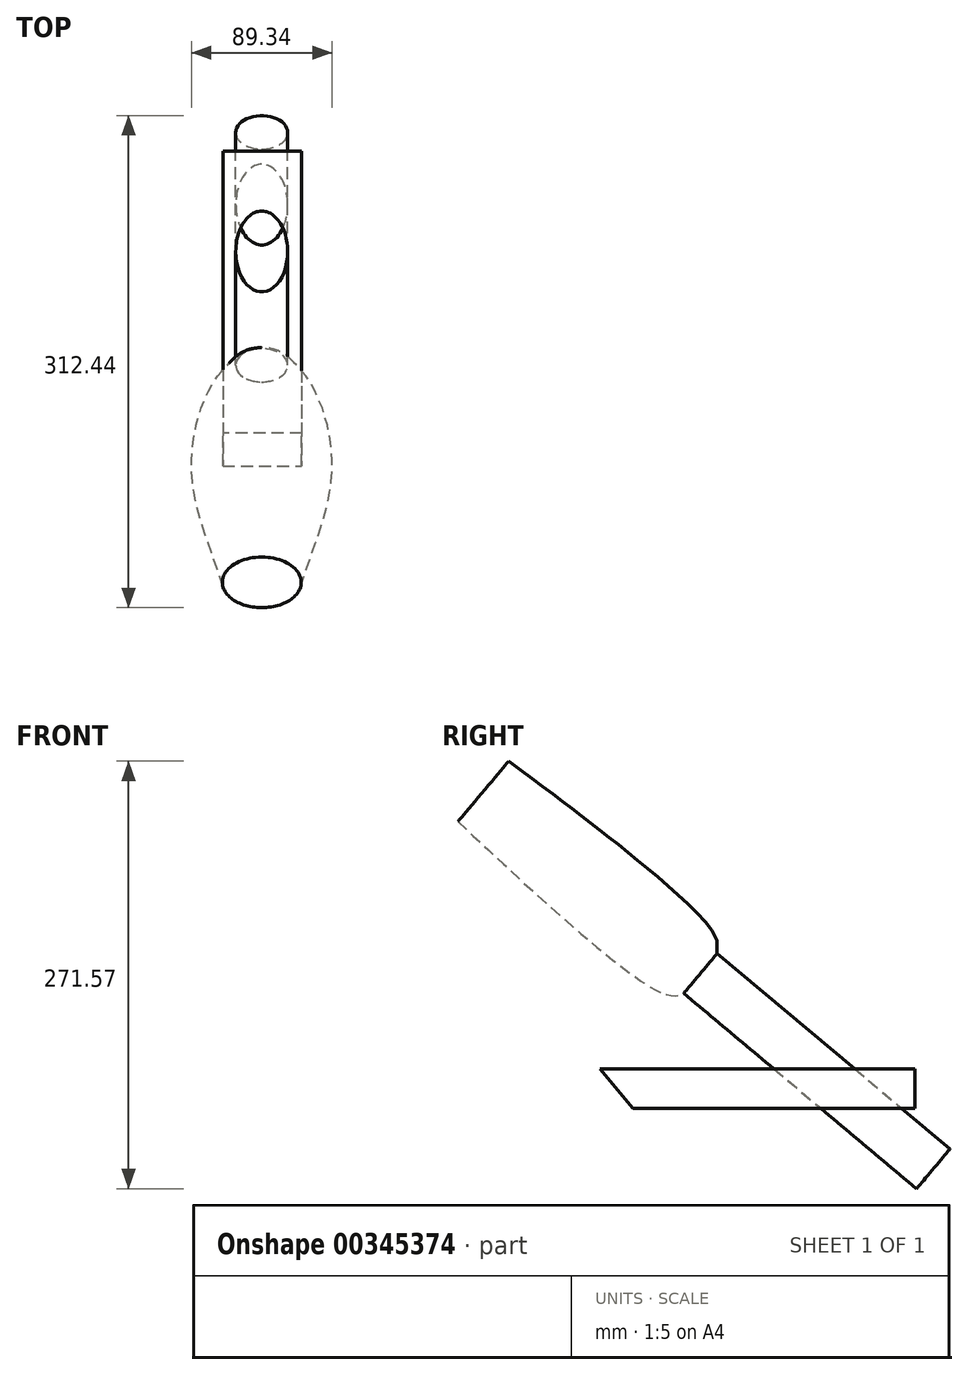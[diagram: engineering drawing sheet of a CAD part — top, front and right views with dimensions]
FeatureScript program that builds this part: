
annotation { "Feature Type Name" : "Feature", "Feature Type Description" : "" }
export const myFeature = defineFeature(function(context is Context, id is Id, definition is map)
    precondition{}
    {
        {
            var Q0;
            Q0=qCreatedBy(makeId("Top.planeOp"),FACE);
            var sketch = newSketch(context, id + "F0", { "sketchPlane" : qUnion([Q0])});
            skLineSegment(sketch, "E0.bottom", {"start": v(-24.67, 141.07) * mm, "end": v(25.33, 141.07) * mm});
            skLineSegment(sketch, "E0.top", {"start": v(-24.67, -58.93) * mm, "end": v(25.33, -58.93) * mm});
            skLineSegment(sketch, "E0.left", {"start": v(-24.67, 141.07) * mm, "end": v(-24.67, -58.93) * mm});
            skLineSegment(sketch, "E0.right", {"start": v(25.33, 141.07) * mm, "end": v(25.33, -58.93) * mm});
            skSolve(sketch);
        }
        {
            var Q0;
            Q0 = qSketchRegion(id + "F0", true);
            extrude(context, id + "F1", {"entities" : qUnion([Q0]), "depth" : 25 * mm});
        }
        {
            var Q0;
            Q0=makeQuery(id+"F1.opExtrude","SWEPT_FACE",FACE,{"disambiguationData":[OSD([sQuery(id+"F0.wireOp",EDGE,"E0.left")])]});
            var sketch = newSketch(context, id + "F2", { "sketchPlane" : qUnion([Q0])});
            skLineSegment(sketch, "E1", {"start": v(58.93, 25) * mm, "end": v(37.96, 0) * mm});
            skLineSegment(sketch, "E2", {"start": v(37.96, 0) * mm, "end": v(58.93, 0) * mm});
            skLineSegment(sketch, "E3", {"start": v(58.93, 0) * mm, "end": v(58.93, 25) * mm});
            skSolve(sketch);
        }
        {
            var Q0;
            Q0=makeQuery(id+"F2.imprint","IMPRINT",FACE,{"disambiguationData":[TD([[makeQuery(id+"F2.imprint","IMPRINT",EDGE,{"derivedFrom":sQuery(id+"F2.wireOp",EDGE,"E1")}),1.0]])]});
            extrude(context, id + "F3", {"entities" : qUnion([Q0]), "operationType" : NewBodyOperationType.REMOVE, "endBound" : BoundingType.UP_TO_NEXT, "oppositeDirection" : true, "depth" : 25 * mm});
        }
        {
            var Q0;
            Q0=qCreatedBy(makeId("Right.planeOp"),FACE);
            var sketch = newSketch(context, id + "F4", { "sketchPlane" : qUnion([Q0])});
            skLineSegment(sketch, "E4", {"start": v(152.85, -38.43) * mm, "end": v(4.97, 85.66) * mm});
            skSolve(sketch);
        }
        {
            var Q0;
            Q0=sQuery(id+"F4.wireOp",EDGE,"E4");
            var Q1;
            Q1=sQuery(id+"F4.wireOp",VERTEX,"E4.end");
            cPlane(context, id + "F5", {"entities" : qUnion([Q0, Q1]), "cplaneType" : CPlaneType.LINE_POINT, "offset" : 25 * mm, "width" : 150 * mm, "height" : 150 * mm});
        }
        {
            var Q0;
            Q0=qCreatedBy(id+"F5.planeOp",FACE);
            var sketch = newSketch(context, id + "F6", { "sketchPlane" : qUnion([Q0])});
            skPoint(sketch, "E5.0", {"position": v(0, 68.81) * mm});
            skCircle(sketch, "E6", {"center": v(0, 68.81) * mm, "radius": 16.5 * mm});
            skSolve(sketch);
        }
        {
            var Q0;
            Q0=makeQuery(id+"F6.imprint","IMPRINT",FACE,{"disambiguationData":[TD([[makeQuery(id+"F6.imprint","IMPRINT",EDGE,{"derivedFrom":sQuery(id+"F6.wireOp",EDGE,"E6")}),1.0]])]});
            var Q1;
            Q1=sQuery(id+"F4.wireOp",EDGE,"E4");
            sweep(context, id + "F7", {"profiles" : qUnion([Q0]), "path" : qUnion([Q1])});
        }
        {
            var Q0;
            Q0=makeQuery(id+"F7.opSweep","CAP_FACE",FACE,{"disambiguationData":[OSD([sQuery(id+"F4.wireOp",VERTEX,"E4.end"),sQuery(id+"F6.wireOp",EDGE,"E6")])],"isStart":true});
            cPlane(context, id + "F8", {"entities" : qUnion([Q0]), "cplaneType" : CPlaneType.OFFSET, "offset" : 10 * mm, "width" : 150 * mm, "height" : 150 * mm});
        }
        {
            var Q0;
            Q0=qCreatedBy(id+"F8.planeOp",FACE);
            var sketch = newSketch(context, id + "F9", { "sketchPlane" : qUnion([Q0])});
            skCircle(sketch, "E7.0.0", {"center": v(0, 68.81) * mm, "radius": 16.5 * mm, "construction": true});
            skCircle(sketch, "E8", {"center": v(0, 68.81) * mm, "radius": 25 * mm});
            skSolve(sketch);
        }
        {
            var Q0;
            Q0=qCreatedBy(id+"F8.planeOp",FACE);
            cPlane(context, id + "F10", {"entities" : qUnion([Q0]), "cplaneType" : CPlaneType.OFFSET, "offset" : 170 * mm, "width" : 150 * mm, "height" : 150 * mm});
        }
        {
            var Q0;
            Q0=qCreatedBy(id+"F10.planeOp",FACE);
            var sketch = newSketch(context, id + "F11", { "sketchPlane" : qUnion([Q0])});
            skPoint(sketch, "E9.0", {"position": v(0, 68.81) * mm});
            skCircle(sketch, "E10", {"center": v(0, 68.81) * mm, "radius": 25 * mm});
            skSolve(sketch);
        }
        {
            var Q0;
            Q0=qCreatedBy(makeId("Right.planeOp"),FACE);
            var sketch = newSketch(context, id + "F12", { "sketchPlane" : qUnion([Q0])});
            skLineSegment(sketch, "E11.0", {"start": v(15.58, 98.3) * mm, "end": v(-5.63, 73.02) * mm});
            skLineSegment(sketch, "E12.0.0", {"start": v(-18.76, 72.93) * mm, "end": v(13.38, 111.24) * mm});
            skLineSegment(sketch, "E13.0", {"start": v(-148.98, 182.2) * mm, "end": v(-116.84, 220.5) * mm});
            skFitSpline(sketch, "E14", {"points": [v(15.58, 98.3) * mm, v(13.38, 111.24) * mm, v(-116.84, 220.5) * mm], "startDerivative": vector(12.66, 54.22) * mm, "endDerivative": vector(-230.77, 171) * mm});
            skFitSpline(sketch, "E15", {"points": [v(-5.63, 73.02) * mm, v(-18.76, 72.93) * mm, v(-148.98, 182.2) * mm], "startDerivative": vector(-51.2, -21.88) * mm, "endDerivative": vector(-208.48, 197.56) * mm});
            skSolve(sketch);
        }
        {
            var Q0;
            Q0=makeQuery(id+"F7.opSweep","CAP_FACE",FACE,{"disambiguationData":[OSD([sQuery(id+"F4.wireOp",VERTEX,"E4.end"),sQuery(id+"F6.wireOp",EDGE,"E6")])],"isStart":true});
            var Q1;
            Q1=makeQuery(id+"F9.imprint","IMPRINT",FACE,{"disambiguationData":[TD([[makeQuery(id+"F9.imprint","IMPRINT",EDGE,{"derivedFrom":sQuery(id+"F9.wireOp",EDGE,"E8")}),1.0]])]});
            var Q2;
            Q2=makeQuery(id+"F11.imprint","IMPRINT",FACE,{"disambiguationData":[TD([[makeQuery(id+"F11.imprint","IMPRINT",EDGE,{"derivedFrom":sQuery(id+"F11.wireOp",EDGE,"E10")}),1.0]])]});
            var Q3;
            Q3=sQuery(id+"F12.wireOp",EDGE,"E14");
            var Q4;
            Q4=sQuery(id+"F12.wireOp",EDGE,"E15");
            loft(context, id + "F13", {"addGuides" : true, "sheetProfilesArray" : [{ "sheetProfileEntities" : qUnion([Q0]) }, { "sheetProfileEntities" : qUnion([Q1]) }, { "sheetProfileEntities" : qUnion([Q2]) }], "guidesArray" : [{ "guideEntities" : qUnion([Q3]), "guideDerivativeType" : LoftGuideDerivativeType.DEFAULT, "guideDerivativeMagnitude" : 1 }, { "guideEntities" : qUnion([Q4]), "guideDerivativeType" : LoftGuideDerivativeType.DEFAULT, "guideDerivativeMagnitude" : 1 }]});
        }
        {
            var Q0;
            Q0=makeQuery(id+"F7.opSweep","SWEPT_BODY",BODY,{"disambiguationData":[OSD([sQuery(id+"F4.wireOp",EDGE,"E4"),sQuery(id+"F6.wireOp",EDGE,"E6")])]});
            var Q1;
            Q1=makeQuery(id+"F1.opExtrude","SWEPT_BODY",BODY,{"disambiguationData":[OSD([sQuery(id+"F0.wireOp",EDGE,"E0.bottom"),sQuery(id+"F0.wireOp",EDGE,"E0.top"),sQuery(id+"F0.wireOp",EDGE,"E0.left"),sQuery(id+"F0.wireOp",EDGE,"E0.right")])]});
            booleanBodies(context, id + "F14", {"operationType" : BooleanOperationType.SUBTRACTION, "tools" : qUnion([Q0]), "targets" : qUnion([Q1]), "keepTools" : true});
        }
    });
